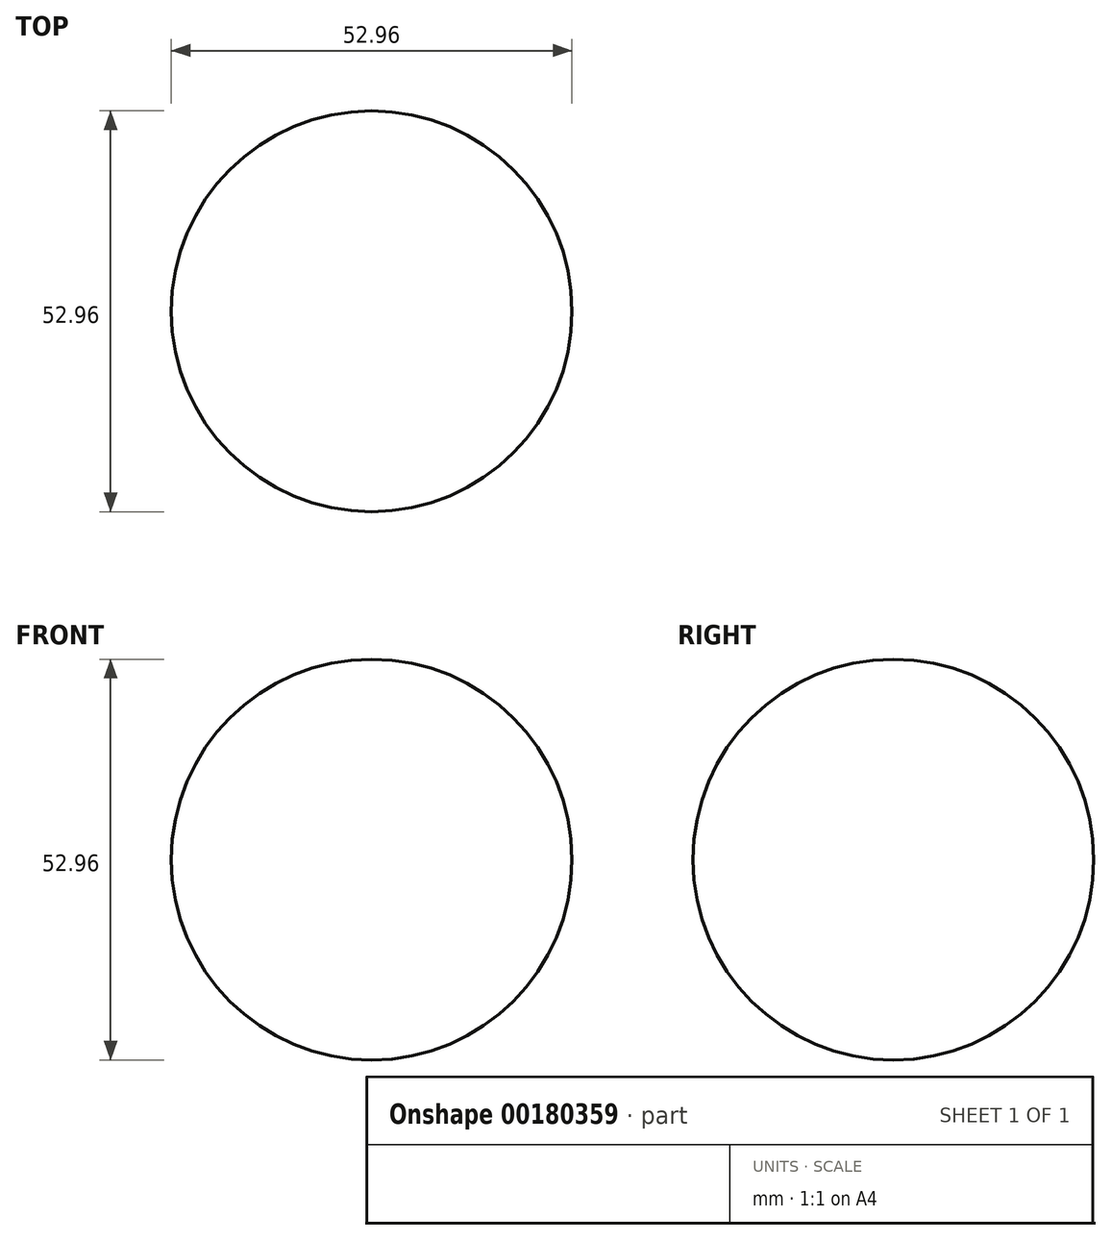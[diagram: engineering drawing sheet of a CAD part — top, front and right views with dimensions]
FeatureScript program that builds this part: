
annotation { "Feature Type Name" : "Feature", "Feature Type Description" : "" }
export const myFeature = defineFeature(function(context is Context, id is Id, definition is map)
    precondition{}
    {
        {
            var Q0;
            Q0=qCreatedBy(makeId("Top.planeOp"),FACE);
            var sketch = newSketch(context, id + "F0", { "sketchPlane" : qUnion([Q0])});
            skCircle(sketch, "E0", {"center": v(0, 0) * mm, "radius": 26.48 * mm});
            skLineSegment(sketch, "E1", {"start": v(0, 0) * mm, "end": v(26.48, 0) * mm});
            skLineSegment(sketch, "E2", {"start": v(26.48, 0) * mm, "end": v(-26.48, 0) * mm});
            skSolve(sketch);
        }
        {
            var Q0;
            {var subQ0=sQuery(id+"F0.wireOp",EDGE,"E2");var subQ4=makeQuery(id+"F0.imprint","IMPRINT",VERTEX,{"derivedFrom":subQ0});Q0=makeQuery(id+"F0.imprint","IMPRINT",FACE,{"disambiguationData":[TD([[makeQuery(id+"F0.imprint","IMPRINT",EDGE,{"disambiguationData":[TD([[subQ4,1.0]])],"derivedFrom":subQ0}),-1.0]])]});}
            var Q1;
            Q1=sQuery(id+"F0.wireOp",EDGE,"E2");
            revolve(context, id + "F1", {"entities" : qUnion([Q0]), "axis" : qUnion([Q1]), "revolveType" : RevolveType.FULL});
        }
    });
